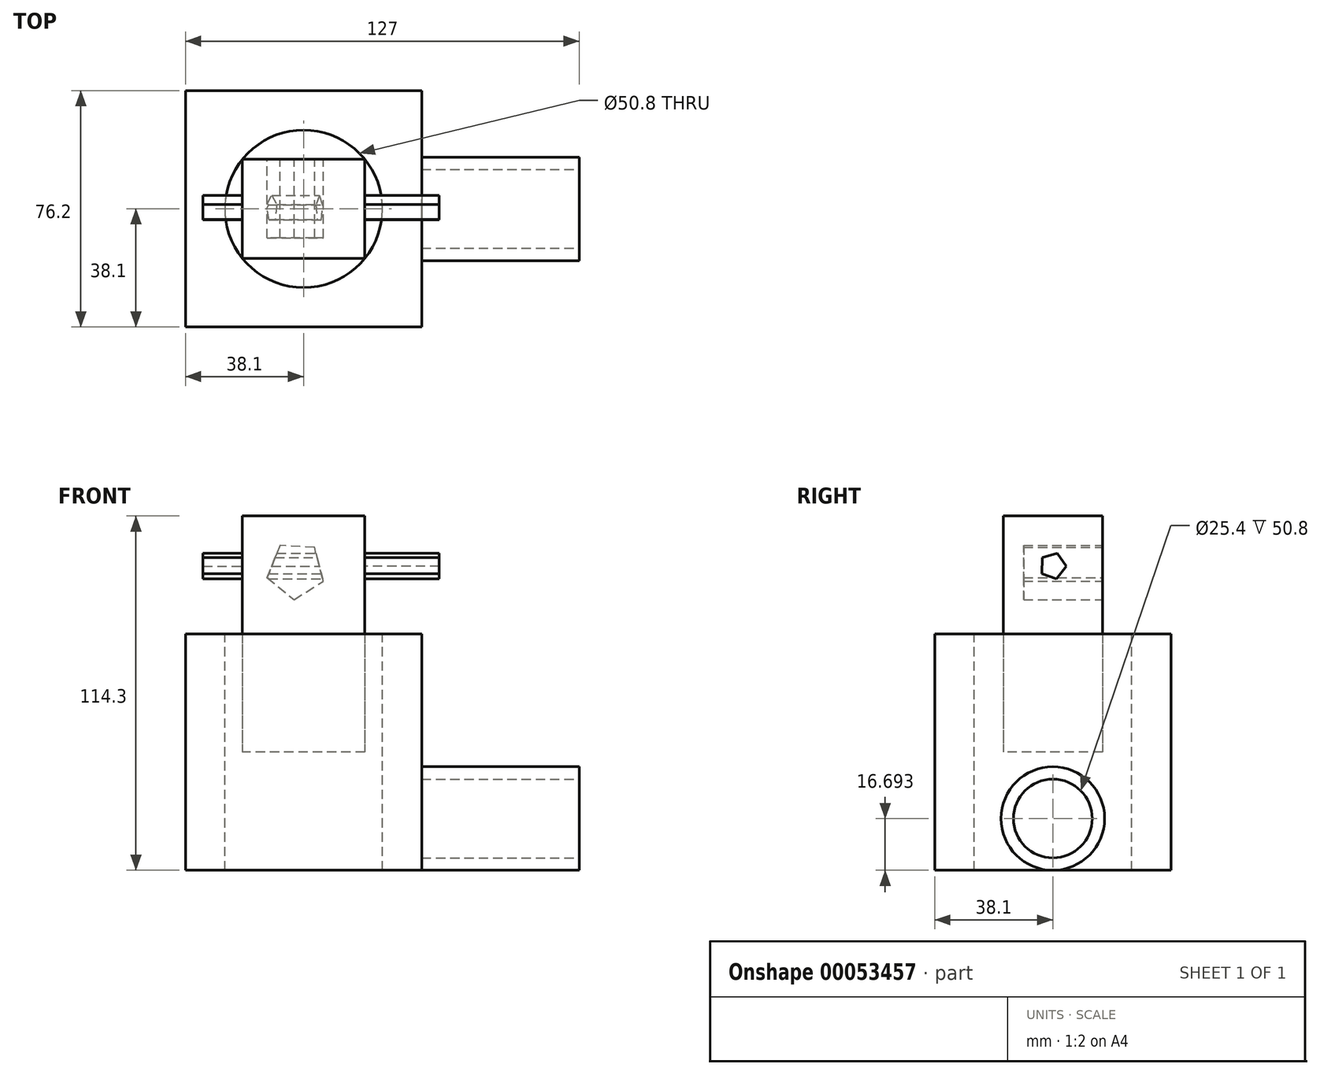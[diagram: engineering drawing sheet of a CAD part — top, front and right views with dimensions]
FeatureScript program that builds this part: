
annotation { "Feature Type Name" : "Feature", "Feature Type Description" : "" }
export const myFeature = defineFeature(function(context is Context, id is Id, definition is map)
    precondition{}
    {
        {
            var Q0;
            Q0=qCreatedBy(makeId("Top.planeOp"),FACE);
            var sketch = newSketch(context, id + "F0", { "sketchPlane" : qUnion([Q0])});
            skLineSegment(sketch, "E0.rect.bottom", {"start": v(38.1, 38.1) * mm, "end": v(-38.1, 38.1) * mm});
            skLineSegment(sketch, "E0.rect.top", {"start": v(38.1, -38.1) * mm, "end": v(-38.1, -38.1) * mm});
            skLineSegment(sketch, "E0.rect.left", {"start": v(38.1, 38.1) * mm, "end": v(38.1, -38.1) * mm});
            skLineSegment(sketch, "E0.rect.right", {"start": v(-38.1, 38.1) * mm, "end": v(-38.1, -38.1) * mm});
            skPoint(sketch, "E0.rect.middle", {"position": v(0, 0) * mm});
            skSolve(sketch);
        }
        {
            var Q0;
            Q0 = qSketchRegion(id + "F0", true);
            extrude(context, id + "F1", {"entities" : qUnion([Q0]), "endBound" : BoundingType.SYMMETRIC, "depth" : 76.2 * mm});
        }
        {
            var Q0;
            Q0=makeQuery(id+"F1.opExtrude","CAP_FACE",FACE,{"disambiguationData":[OSD([sQuery(id+"F0.wireOp",EDGE,"E0.rect.bottom"),sQuery(id+"F0.wireOp",EDGE,"E0.rect.top"),sQuery(id+"F0.wireOp",EDGE,"E0.rect.left"),sQuery(id+"F0.wireOp",EDGE,"E0.rect.right")])],"isStart":false});
            var sketch = newSketch(context, id + "F2", { "sketchPlane" : qUnion([Q0])});
            skCircle(sketch, "E1", {"center": v(0, 0) * mm, "radius": 25.4 * mm});
            skSolve(sketch);
        }
        {
            var Q0;
            Q0 = qSketchRegion(id + "F2", true);
            var Q1;
            Q1=makeQuery(id+"F1.opExtrude","CAP_FACE",FACE,{"disambiguationData":[OSD([sQuery(id+"F0.wireOp",EDGE,"E0.rect.bottom"),sQuery(id+"F0.wireOp",EDGE,"E0.rect.top"),sQuery(id+"F0.wireOp",EDGE,"E0.rect.left"),sQuery(id+"F0.wireOp",EDGE,"E0.rect.right")])],"isStart":true});
            extrude(context, id + "F3", {"entities" : qUnion([Q0]), "operationType" : NewBodyOperationType.REMOVE, "endBound" : BoundingType.THROUGH_ALL, "oppositeDirection" : true, "endBoundEntityFace" : qUnion([Q1]), "depth" : 25.4 * mm});
        }
        {
            var Q0;
            Q0=makeQuery(id+"F1.opExtrude","CAP_FACE",FACE,{"disambiguationData":[OSD([sQuery(id+"F0.wireOp",EDGE,"E0.rect.bottom"),sQuery(id+"F0.wireOp",EDGE,"E0.rect.top"),sQuery(id+"F0.wireOp",EDGE,"E0.rect.left"),sQuery(id+"F0.wireOp",EDGE,"E0.rect.right")])],"isStart":false});
            var sketch = newSketch(context, id + "F4", { "sketchPlane" : qUnion([Q0])});
            skLineSegment(sketch, "E2.rect.bottom", {"start": v(19.73, 16) * mm, "end": v(-19.73, 16) * mm});
            skLineSegment(sketch, "E2.rect.top", {"start": v(19.73, -16) * mm, "end": v(-19.73, -16) * mm});
            skLineSegment(sketch, "E2.rect.left", {"start": v(19.73, 16) * mm, "end": v(19.73, -16) * mm});
            skLineSegment(sketch, "E2.rect.right", {"start": v(-19.73, 16) * mm, "end": v(-19.73, -16) * mm});
            skPoint(sketch, "E2.rect.middle", {"position": v(0, 0) * mm});
            skSolve(sketch);
        }
        {
            var Q0;
            Q0=makeQuery(id+"F4.imprint","IMPRINT",FACE,{"disambiguationData":[TD([[makeQuery(id+"F4.imprint","IMPRINT",EDGE,{"derivedFrom":sQuery(id+"F4.wireOp",EDGE,"E2.rect.bottom")}),1.0]])]});
            extrude(context, id + "F5", {"entities" : qUnion([Q0]), "endBound" : BoundingType.SYMMETRIC, "depth" : 76.2 * mm});
        }
        {
            var Q0;
            Q0=makeQuery(id+"F5.opExtrude","SWEPT_FACE",FACE,{"disambiguationData":[OSD([sQuery(id+"F4.wireOp",EDGE,"E2.rect.bottom")])]});
            var sketch = newSketch(context, id + "F6", { "sketchPlane" : qUnion([Q0])});
            skCircle(sketch, "E3.cCircle", {"center": v(2.52, 58.68) * mm, "radius": 9.52 * mm, "construction": true});
            skLineSegment(sketch, "E3.0", {"start": v(3.08, 49.17) * mm, "end": v(-6.35, 55.2) * mm});
            skLineSegment(sketch, "E3.1", {"start": v(-6.35, 55.2) * mm, "end": v(-3.52, 66.04) * mm});
            skLineSegment(sketch, "E3.2", {"start": v(-3.52, 66.04) * mm, "end": v(7.66, 66.7) * mm});
            skLineSegment(sketch, "E3.3", {"start": v(7.66, 66.7) * mm, "end": v(11.73, 56.27) * mm});
            skLineSegment(sketch, "E3.4", {"start": v(11.73, 56.27) * mm, "end": v(3.08, 49.17) * mm});
            skSolve(sketch);
        }
        {
            var Q0;
            Q0 = qSketchRegion(id + "F6", true);
            extrude(context, id + "F7", {"entities" : qUnion([Q0]), "operationType" : NewBodyOperationType.REMOVE, "oppositeDirection" : true, "depth" : 25.4 * mm});
        }
        {
            var Q0;
            Q0=makeQuery(id+"F5.opExtrude","SWEPT_FACE",FACE,{"disambiguationData":[OSD([sQuery(id+"F4.wireOp",EDGE,"E2.rect.right")])]});
            var sketch = newSketch(context, id + "F8", { "sketchPlane" : qUnion([Q0])});
            skCircle(sketch, "E4.cCircle", {"center": v(0, 60.08) * mm, "radius": 4.35 * mm, "construction": true});
            skLineSegment(sketch, "E4.0", {"start": v(-4.35, 59.97) * mm, "end": v(-1.45, 64.18) * mm});
            skLineSegment(sketch, "E4.1", {"start": v(-1.45, 64.18) * mm, "end": v(3.45, 62.73) * mm});
            skLineSegment(sketch, "E4.2", {"start": v(3.45, 62.73) * mm, "end": v(3.58, 57.62) * mm});
            skLineSegment(sketch, "E4.3", {"start": v(3.58, 57.62) * mm, "end": v(-1.24, 55.91) * mm});
            skLineSegment(sketch, "E4.4", {"start": v(-1.24, 55.91) * mm, "end": v(-4.35, 59.97) * mm});
            skSolve(sketch);
        }
        {
            var Q0;
            Q0=makeQuery(id+"F8.imprint","IMPRINT",FACE,{"disambiguationData":[TD([[makeQuery(id+"F8.imprint","IMPRINT",EDGE,{"derivedFrom":sQuery(id+"F8.wireOp",EDGE,"E4.0")}),-1.0]])]});
            extrude(context, id + "F9", {"entities" : qUnion([Q0]), "operationType" : NewBodyOperationType.ADD, "endBound" : BoundingType.SYMMETRIC, "depth" : 25.4 * mm});
        }
        {
            var Q0;
            Q0=makeQuery(id+"F9.opExtrude","CAP_FACE",FACE,{"disambiguationData":[OSD([sQuery(id+"F8.wireOp",EDGE,"E4.0"),sQuery(id+"F8.wireOp",EDGE,"E4.1"),sQuery(id+"F8.wireOp",EDGE,"E4.2"),sQuery(id+"F8.wireOp",EDGE,"E4.3"),sQuery(id+"F8.wireOp",EDGE,"E4.4")])],"isStart":true});
            extrude(context, id + "F10", {"entities" : qUnion([Q0]), "operationType" : NewBodyOperationType.ADD, "depth" : 50.8 * mm});
        }
        {
            var Q0;
            Q0=makeQuery(id+"F1.opExtrude","SWEPT_FACE",FACE,{"disambiguationData":[OSD([sQuery(id+"F0.wireOp",EDGE,"E0.rect.left")])]});
            var sketch = newSketch(context, id + "F11", { "sketchPlane" : qUnion([Q0])});
            skCircle(sketch, "E5", {"center": v(0, -21.4) * mm, "radius": 16.7 * mm});
            skSolve(sketch);
        }
        {
            var Q0;
            Q0=makeQuery(id+"F11.imprint","IMPRINT",FACE,{"disambiguationData":[TD([[makeQuery(id+"F11.imprint","IMPRINT",EDGE,{"derivedFrom":sQuery(id+"F11.wireOp",EDGE,"E5")}),1.0]])]});
            extrude(context, id + "F12", {"entities" : qUnion([Q0]), "operationType" : NewBodyOperationType.ADD, "depth" : 50.8 * mm});
        }
        {
            var Q0;
            Q0=makeQuery(id+"F12.opExtrude","CAP_FACE",FACE,{"disambiguationData":[OSD([sQuery(id+"F11.wireOp",EDGE,"E5")])],"isStart":false});
            var sketch = newSketch(context, id + "F13", { "sketchPlane" : qUnion([Q0])});
            skCircle(sketch, "E6", {"center": v(0, -21.4) * mm, "radius": 12.7 * mm});
            skSolve(sketch);
        }
        {
            var Q0;
            Q0=makeQuery(id+"F13.imprint","IMPRINT",FACE,{"disambiguationData":[TD([[makeQuery(id+"F13.imprint","IMPRINT",EDGE,{"derivedFrom":sQuery(id+"F13.wireOp",EDGE,"E6")}),1.0]])]});
            extrude(context, id + "F14", {"entities" : qUnion([Q0]), "operationType" : NewBodyOperationType.REMOVE, "oppositeDirection" : true, "depth" : 50.8 * mm});
        }
    });
